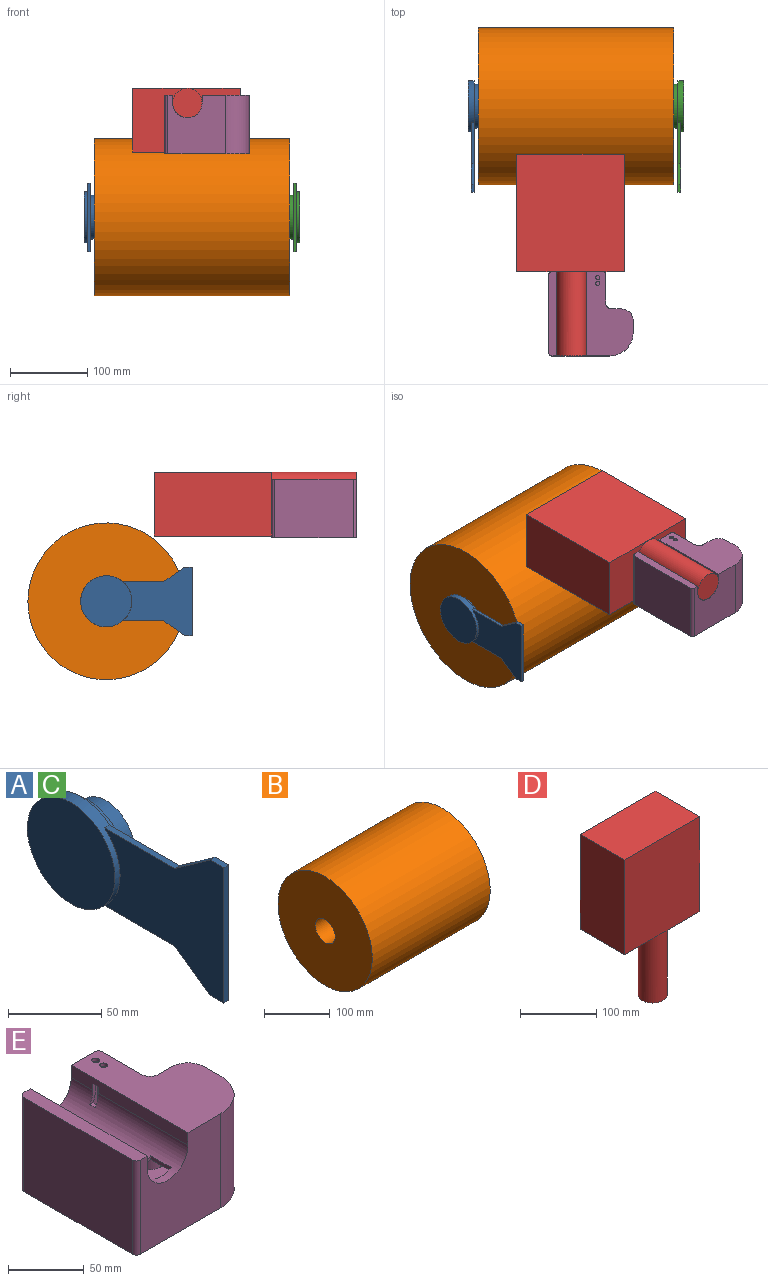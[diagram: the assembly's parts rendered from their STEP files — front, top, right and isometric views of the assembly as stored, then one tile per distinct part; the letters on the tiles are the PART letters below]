
ASSEMBLY  parts=5 mates=4
PART A: 15 faces, bbox 26.3x144.6x88.6 mm
  f0: cylinder r=21.46mm len=42.93mm, axis (-1,0,0), area 1832.6mm2, adj f1,f3
  f1: plane 42.93x42.93mm, normal (1,0,0), area 1447.2mm2, adj f0
  f2: cylinder r=28.7mm len=57.4mm, axis (1,0,0), area 916.1mm2, adj f3,f6
  f3: plane 57.4x57.4mm, normal (1,0,0), area 1140.9mm2, adj f0,f2
  f4: cylinder r=33.15mm len=66.29mm, axis (1,0,0), area 1369.4mm2, adj f5,f6,f7,f13,f14
  f5: plane 66.29x66.29mm, normal (-1,0,0), area 3451.7mm2, adj f4
  f6: plane 144.61x88.65mm, normal (1,0,0), area 5915.2mm2, adj f2,f4,f7,f8,f9,f10,f11,f12
  f7: plane 53.34x3.76mm, normal (0,0,-1), area 200.5mm2, adj f4,f6,f8,f14
  f8: plane 26.67x18.92mm, normal (0,0.58,-0.82), area 122.9mm2, adj f6,f7,f9,f14
  f9: plane 10.16x3.76mm, normal (0,0,-1), area 38.2mm2, adj f6,f8,f10,f14
  f10: plane 88.65x3.76mm, normal (0,-1,0), area 333.2mm2, adj f6,f9,f11,f14
  f11: plane 10.16x3.76mm, normal (0,0,1), area 38.2mm2, adj f6,f10,f12,f14
  f12: plane 26.67x18.92mm, normal (0,0.58,0.82), area 122.9mm2, adj f6,f11,f13,f14
  f13: plane 53.34x3.76mm, normal (0,0,1), area 200.5mm2, adj f4,f6,f12,f14
  f14: plane 90.17x88.65mm, normal (-1,0,0), area 5051.5mm2, adj f4,f7,f8,f9,f10,f11,f12,f13
PART B: 4 faces, bbox 254x203.2x203.2 mm
  f0: cylinder r=101.6mm len=254mm, axis (-1,0,0), area 162146.4mm2, adj f1,f2
  f1: plane 203.2x203.2mm, normal (1,0,0), area 30982.1mm2, adj f0,f3
  f2: plane 203.2x203.2mm, normal (-1,0,0), area 30982.1mm2, adj f0,f3
  f3: cylinder r=21.46mm len=254mm, axis (-1,0,0), area 34253.4mm2, adj f1,f2
PART C: same geometry as A
PART D: 8 faces, bbox 139.7x82.6x261.6 mm
  f0: plane 152.4x82.55mm, normal (-1,0,0), area 12580.6mm2, adj f1,f3,f4,f5
  f1: plane 139.7x82.55mm, normal (0,0,-1), area 10392.1mm2, adj f0,f2,f4,f5,f6
  f2: plane 152.4x82.55mm, normal (1,0,0), area 12580.6mm2, adj f1,f3,f4,f5
  f3: plane 139.7x82.55mm, normal (0,0,1), area 11532.2mm2, adj f0,f2,f4,f5
  f4: plane 152.4x139.7mm, normal (0,1,0), area 21290.3mm2, adj f0,f1,f2,f3
  f5: plane 152.4x139.7mm, normal (0,-1,0), area 21290.3mm2, adj f0,f1,f2,f3
  f6: cylinder r=19.05mm len=109.22mm, axis (0,0,1), area 13073.1mm2, adj f1,f7
  f7: plane 38.1x38.1mm, normal (0,0,-1), area 1140.1mm2, adj f6
PART E: 46 faces, bbox 109.2x109.2x76.2 mm
  f0: cylinder r=21.59mm len=104.14mm, axis (0,1,0), area 6633.9mm2, adj f1,f5,f11,f19,f20,f21,f22,f23
  f1: plane 104.14x7.62mm, normal (1,0,0), area 767.7mm2, adj f0,f5,f11,f17,f43,f44,f45
  f2: cylinder r=19.05mm len=109.22mm, axis (0,1,0), area 6102.1mm2, adj f3,f20,f21,f22,f23,f25,f31,f39
  f3: plane 109.22x10.16mm, normal (-1,0,0), area 1083.9mm2, adj f2,f25,f31,f37,f43,f44,f45
  f4: plane 104.14x5.08mm, normal (0,0,-1), area 528.3mm2, adj f5,f8,f9,f10,f11,f19
  f5: plane 71.12x66.04mm, normal (0,-1,0), area 3635.5mm2, adj f0,f1,f4,f7,f8,f17,f18,f19
  f6: plane 71.12x36.83mm, normal (-1,0,0), area 2619.3mm2, adj f7,f16,f17,f18
  f7: cylinder r=1.27mm len=71.12mm, axis (0,0,-1), area 141.9mm2, adj f5,f6,f17,f18
  f8: cylinder r=1.27mm len=71.12mm, axis (0,0,-1), area 141.9mm2, adj f4,f5,f9,f18
  f9: plane 101.6x71.12mm, normal (1,0,0), area 7225.8mm2, adj f4,f8,f10,f18
  f10: cylinder r=1.27mm len=71.12mm, axis (0,0,-1), area 141.9mm2, adj f4,f9,f11,f18
  f11: plane 74.93x71.12mm, normal (0,1,0), area 4267.8mm2, adj f0,f1,f4,f10,f12,f17,f18,f19
  f12: cylinder r=27.94mm len=71.12mm, axis (0,0,-1), area 3121.3mm2, adj f11,f13,f17,f18
  f13: plane 71.12x15.24mm, normal (-1,0,0), area 1083.9mm2, adj f12,f14,f17,f18
  f14: cylinder r=12.7mm len=71.12mm, axis (0,0,-1), area 1418.8mm2, adj f13,f15,f17,f18
  f15: plane 71.12x12.7mm, normal (0,-1,0), area 903.2mm2, adj f14,f16,f17,f18
  f16: cylinder r=10.16mm len=71.12mm, axis (0,0,-1), area 1135mm2, adj f6,f15,f17,f18
  f17: plane 104.14x55.88mm, normal (0,0,-1), area 3882.3mm2, adj f1,f5,f6,f7,f11,f12,f13,f14
  f18: plane 104.14x104.14mm, normal (0,0,1), area 8948mm2, adj f5,f6,f7,f8,f9,f10,f11,f12
  f19: plane 104.14x7.62mm, normal (-1,0,0), area 793.5mm2, adj f0,f4,f5,f11
  f20: plane 19.05x2.88mm, normal (-1,0,0), area 54.8mm2, adj f0,f2,f21,f23
  f21: plane 19.05x5.09mm, normal (0,-1,0), area 50.4mm2, adj f0,f2,f20,f22
  f22: plane 19.05x2.88mm, normal (1,0,0), area 54.8mm2, adj f0,f2,f21,f23
  f23: plane 19.05x5.09mm, normal (0,1,0), area 50.4mm2, adj f0,f2,f20,f22
  f24: plane 109.22x10.16mm, normal (0,0,1), area 1103.4mm2, adj f25,f28,f29,f30,f31,f39
  f25: plane 76.2x66.04mm, normal (0,1,0), area 4075.1mm2, adj f2,f3,f24,f27,f28,f37,f38,f39
  f26: plane 76.2x36.83mm, normal (1,0,0), area 2806.4mm2, adj f27,f36,f37,f38
  f27: cylinder r=3.81mm len=76.2mm, axis (0,0,-1), area 456mm2, adj f25,f26,f37,f38
  f28: cylinder r=3.81mm len=76.2mm, axis (0,0,-1), area 456mm2, adj f24,f25,f29,f38
  f29: plane 101.6x76.2mm, normal (-1,0,0), area 7741.9mm2, adj f24,f28,f30,f38
  f30: cylinder r=3.81mm len=76.2mm, axis (0,0,-1), area 456mm2, adj f24,f29,f31,f38
  f31: plane 76.2x74.93mm, normal (0,-1,0), area 4752.5mm2, adj f2,f3,f24,f30,f32,f37,f38,f39
  f32: cylinder r=30.48mm len=76.2mm, axis (0,0,-1), area 3648.3mm2, adj f31,f33,f37,f38
  f33: plane 76.2x15.24mm, normal (1,0,0), area 1161.3mm2, adj f32,f34,f37,f38
  f34: cylinder r=15.24mm len=76.2mm, axis (0,0,-1), area 1824.1mm2, adj f33,f35,f37,f38
  f35: plane 76.2x12.7mm, normal (0,1,0), area 967.7mm2, adj f34,f36,f37,f38
  f36: cylinder r=7.62mm len=76.2mm, axis (0,0,-1), area 912.1mm2, adj f26,f35,f37,f38
  f37: plane 109.22x60.96mm, normal (0,0,1), area 4661.5mm2, adj f3,f25,f26,f27,f31,f32,f33,f34
  f38: plane 109.22x109.22mm, normal (0,0,-1), area 9966.8mm2, adj f25,f26,f27,f28,f29,f30,f31,f32
  f39: plane 109.22x10.16mm, normal (1,0,0), area 1109.7mm2, adj f2,f24,f25,f31
  f40: cylinder r=2.54mm len=5.08mm, axis (0,0,1), area 40.5mm2, adj f17,f37
  f41: cylinder r=2.54mm len=5.08mm, axis (0,0,1), area 40.5mm2, adj f17,f37
  f42: plane 5.08x2.94mm, normal (0,0,1), area 14.9mm2, adj f0,f2,f43,f44
  f43: plane 15.24x5.48mm, normal (0,1,0), area 39.9mm2, adj f0,f1,f2,f3,f42,f45
  f44: plane 15.24x5.48mm, normal (0,-1,0), area 39.9mm2, adj f0,f1,f2,f3,f42,f45
  f45: plane 5.08x2.54mm, normal (0,0,-1), area 12.9mm2, adj f1,f3,f43,f44
PLACE A rot(axis=(0,1,0),0deg) t=(-119.76,62.18,-167.18)mm
PLACE B rot(axis=(0,-1,0),180deg) t=(7.24,62.18,-167.18)mm
PLACE C rot(axis=(0,-1,0),180deg) t=(134.24,62.18,-167.18)mm
PLACE D rot(axis=(-1,0,0),90deg) t=(1.29,-93.58,0)mm fixed
PLACE E t=(26.69,-207.01,-85.09)mm
MATE fastened A.f0 <-> B.f0  axis (1,0,0) through (-119.76,62.18,-167.18)mm
MATE parallel D.f3 <-> A.f10  axis (0,1,0) through (0,0,-41.28)mm
MATE fastened D.f6 <-> E.f0  axis (0,1,0) through (1.29,-207.01,-19.05)mm
MATE fastened C.f0 <-> B.f0  axis (-1,0,0) through (134.24,62.18,-167.18)mm
